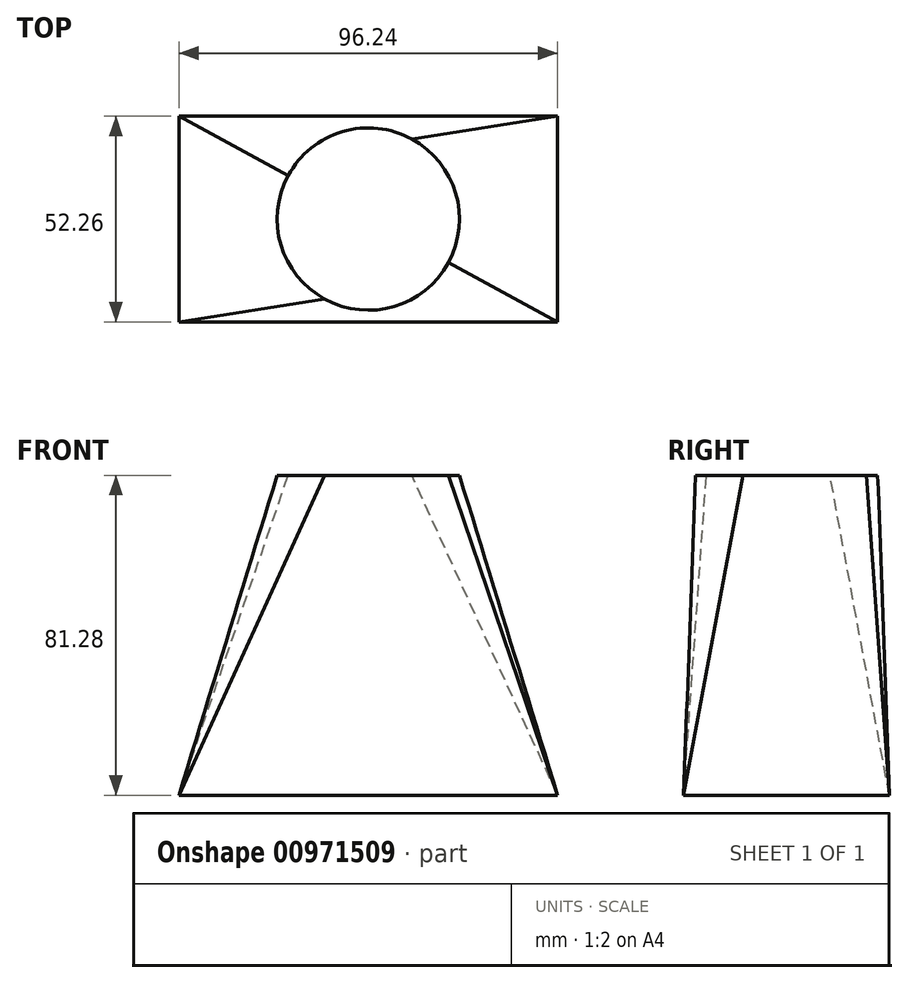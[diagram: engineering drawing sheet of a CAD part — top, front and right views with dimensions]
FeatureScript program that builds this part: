
annotation { "Feature Type Name" : "Feature", "Feature Type Description" : "" }
export const myFeature = defineFeature(function(context is Context, id is Id, definition is map)
    precondition{}
    {
        {
            var Q0;
            Q0=qCreatedBy(makeId("Top.planeOp"),FACE);
            var sketch = newSketch(context, id + "F0", { "sketchPlane" : qUnion([Q0])});
            skLineSegment(sketch, "E0.bottom", {"start": v(-48.12, 26.13) * mm, "end": v(48.12, 26.13) * mm});
            skLineSegment(sketch, "E0.top", {"start": v(-48.12, -26.13) * mm, "end": v(48.12, -26.13) * mm});
            skLineSegment(sketch, "E0.left", {"start": v(-48.12, 26.13) * mm, "end": v(-48.12, -26.13) * mm});
            skLineSegment(sketch, "E0.right", {"start": v(48.12, 26.13) * mm, "end": v(48.12, -26.13) * mm});
            skPoint(sketch, "E0.middle", {"position": v(0, 0) * mm});
            skSolve(sketch);
        }
        {
            var Q0;
            Q0=qCreatedBy(makeId("Top.planeOp"),FACE);
            cPlane(context, id + "F1", {"entities" : qUnion([Q0]), "cplaneType" : CPlaneType.OFFSET, "offset" : 81.28 * mm, "width" : 152.4 * mm, "height" : 152.4 * mm});
        }
        {
            var Q0;
            Q0=qCreatedBy(id+"F1.planeOp",FACE);
            var sketch = newSketch(context, id + "F2", { "sketchPlane" : qUnion([Q0])});
            skCircle(sketch, "E1", {"center": v(0, 0) * mm, "radius": 23.16 * mm});
            skSolve(sketch);
        }
        {
            var Q0;
            Q0=makeQuery(id+"F0.imprint","IMPRINT",FACE,{"disambiguationData":[TD([[makeQuery(id+"F0.imprint","IMPRINT",EDGE,{"derivedFrom":sQuery(id+"F0.wireOp",EDGE,"E0.bottom")}),-1.0]])]});
            var Q1;
            Q1=makeQuery(id+"F2.imprint","IMPRINT",FACE,{"disambiguationData":[TD([[makeQuery(id+"F2.imprint","IMPRINT",EDGE,{"derivedFrom":sQuery(id+"F2.wireOp",EDGE,"E1")}),1.0]])]});
            loft(context, id + "F3", {"sheetProfilesArray" : [{ "sheetProfileEntities" : qUnion([Q0]) }, { "sheetProfileEntities" : qUnion([Q1]) }]});
        }
    });
